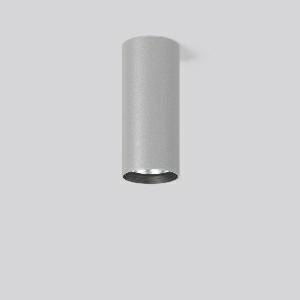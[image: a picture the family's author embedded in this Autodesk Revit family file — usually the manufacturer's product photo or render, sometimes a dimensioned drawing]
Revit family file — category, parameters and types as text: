
# Revit family: heledon_mini_a_931201_004_3_76_e9dc
name_source: partatom
category: Lighting Fixtures
units: mm (PartAtom-declared; Revit-internal decimal feet)

## family parameters
Cut with Voids When Loaded = No
Host = Face
Light Source = No
Part Type = Normal
Room Calculation Point = No
Round Connector Dimension = Use Diameter
Shared = No

## types (1)
- HELEDON mini A (1 x LED Modul 935, 2500 lm, 3500)
    Apparent Load = 20 VA
    Approval mark = CE
    CIE Flux Codes = 99 100 100 100 100
    Color Rendering = 92
    Color Temperature = 3500
    Default Elevation = 1800 mm
    Description = Series: HELEDON mini
Cylindrical surface-mounted downlight. Housing: die-cast aluminium, powder-coated. Internal ceiling frame polycarbonate with bayonet mounting. Black plastic ring and recessed LED to prevent glare from the side. Optical assembly with reflector made of MIRO-Silver with 98% total light reflection for outstanding efficiency - can be changed without tools. Best colour rendering index Ra>90. Suitable for Ceiling mounting. Easy installation with a separate ceiling frame with bayonet mounting and plug connection. Driver integrated. Connected via plug-in connector. High quality converter without flickering and stroboscopic effect. The following accessories can be mounted without use of tools: interchangeable lenses, decorative glasses, honeycomb louvre, clear and frosted diffusers, white interchangeable plastic ring. 
Colour: silver
Diameter: 87 mm
Height: 197 mm
Lamp: LED
Socket: without socket
Colour temperature: 3500K
Colour rendering index (CRI): 92
System power: 20 W
Rated luminous flux: 2500 lm
Luminous efficiency: 125 lm/W
Control gear: Converter, dimmable, DALI
Protection class: I
Type of protection: IP 20
    Height = 197 mm
    Lamp = 1 x LED Modul 935
    Lamp Light Flux = 2500 lm
    Lamp count = 1
    Length = 87 mm
    Lifetime = 50000 h
    Luminous efficacy = 125 lm/W
    Manufacturer = RZB
    ModVariant = No
    Model = 931201.004.3.76
    Mounting Place = Ceiling
    Mounting Type = Surface mounted
    Number of Poles = 1
    OnlyDefault = Yes
    Power Factor = 1
    Product Name = HELEDON mini A
    Product group = Surface mounted downlights
    ProductGroupID = 302
    Protection Class = Protection class I
    Protection Degree = IP 20
    RLX_Detail_Level = 1
    RLX_Emergency_Light_Flux = 0 lm
    RLX_Emergency_Type = 0
    RLX_Emergency_Type_DB = No
    RlxData = <blob elided: 107513 chars, md5=e23426f2>
    Socket = socket
    Standby Power = 0 W
    System Light Flux = 2500 lm
    System Power = 20 W
    Type Comments = Product without accessories
    Type Image = 931188.004.jpg
    URL = http://relux.com
    VarID = ---
    Voltage = 230 V
    Voltage Range = 220-240 V
    Weight = 0.00 kg
    Width = 0 mm  [stored 0 ft]

note: [stored X ft] marks values corroborated as IEEE doubles in the binary element streams (Revit-internal decimal feet)

## geometry (parser evidence)
native form markers: Blend x4, Sweep x9
no freeform markers — native parametric forms only
